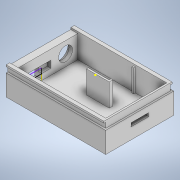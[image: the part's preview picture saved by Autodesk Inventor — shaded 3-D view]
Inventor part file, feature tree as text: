
AUTODESK INVENTOR PART (.ipt)
format: ipt  version: 2021 (Build 250183000, 183)  size: 361,984 bytes
history: native  units: mm
features: sketch x27, extrude x23, other x1
ambient origin geometry x8: Origin, YZ Plane, XZ Plane, XY Plane, X Axis, Y Axis, Z Axis, Center Point
bodies: Body1 (feature_tree)
feature tree (51):
  other  "Sólido1"
  extrude  "Extrusión1"  Depth=35.0mm
  extrude  "Extrusión2"  Depth=51.0mm
  sketch  "Boceto3"  dims[d5=31.0mm d6=13.0mm d7=0.0mm]
  extrude  "Extrusión3"  Depth=13.0mm TaperAngle=0.0deg
  extrude  "Extrusión4"  Depth=15.0mm TaperAngle=0.0deg
  extrude  "Extrusión5"  Depth=6.5mm
  extrude  "Extrusión6"  Depth=2.0mm TaperAngle=0.0deg
  extrude  "Extrusión7"  Depth=2.0mm TaperAngle=0.0deg
  extrude  "Extrusión8"  Depth=32.0mm
  extrude  "Extrusión9"  Depth=13.0mm TaperAngle=0.0deg
  extrude  "Extrusión10"  Depth=15.0mm TaperAngle=0.0deg
  sketch  "Boceto12"  dims[d41=10.0mm d45=3.0mm]
  extrude  "Extrusión11"  Depth=13.0mm TaperAngle=0.0deg
  extrude  "Extrusión12"  Depth=3.0mm
  sketch  "Boceto15"  dims[d55=19.0mm d56=3.0mm]
  sketch  "Boceto16"  dims[d57=2.0mm d58=0.0mm d59=19.5mm]
  extrude  "Extrusión13"  Depth=4.0mm TaperAngle=0.0deg
  extrude  "Extrusión14"  Depth=3.0mm
  extrude  "Extrusión15"  Depth=3.0mm
  extrude  "Extrusión16"  Depth=19.5mm
  extrude  "Extrusión17"  Depth=5.0mm
  extrude  "Extrusión18"  Depth=10.0mm
  extrude  "Extrusión19"  Depth=2.0mm
  extrude  "Extrusión20"  Depth=1.0mm
  extrude  "Extrusión21"  Depth=37.0mm
  extrude  "Extrusión22"  Depth=1.0mm TaperAngle=0.0deg
  sketch  "Boceto26"  dims[d82=0.5mm]
  extrude  "Extrusión23"  Depth=8.0mm
  sketch  "Boceto1"  dims[d0=55.0mm d1=35.0mm]
  sketch  "Boceto2"  dims[d2=15.0mm d3=0.0mm d4=51.0mm]
  sketch  "Boceto4"  dims[d8=2.0mm d9=15.0mm d10=0.0mm]
  sketch  "Boceto5"  dims[d11=9.0mm d12=6.5mm]
  sketch  "Boceto6"  dims[d13=11.0mm d14=2.0mm d15=0.0mm]
  sketch  "Boceto7"  dims[d16=8.0mm d17=2.0mm d18=0.0mm]
  sketch  "Boceto8"  dims[d19=7.0mm d27=32.0mm]
  sketch  "Boceto9"  dims[d28=13.0mm d29=0.0mm d32=13.0mm d33=0.0mm]
  sketch  "Boceto10"  dims[d34=4.0mm d35=15.0mm d36=0.0mm]
  sketch  "Boceto11"  dims[d37=4.0mm d38=13.0mm d39=0.0mm]
  sketch  "Boceto13"  dims[d46=4.0mm d48=4.0mm d49=0.0mm]
  sketch  "Boceto14"  dims[d52=9.5mm d54=3.0mm]
  sketch  "Boceto17"  dims[d60=7.5mm d61=5.0mm]
  sketch  "Boceto18"  dims[d62=1.0mm d63=10.0mm]
  sketch  "Boceto19"  dims[d64=2.0mm d65=2.0mm]
  sketch  "Boceto20"  dims[d66=3.0mm d67=0.0mm d69=1.0mm]
  sketch  "Boceto21"  dims[d70=55.0mm d71=37.0mm]
  sketch  "Boceto22"  dims[d72=3.0mm d73=0.0mm d74=1.0mm d75=0.0mm]
  sketch  "Boceto23"  dims[d76=1.0mm d77=0.0mm d78=8.0mm]
  sketch  "Boceto24"  dims[d79=3.0mm]
  sketch  "Boceto25"  dims[d80=6.0mm d81=0.0mm]
  sketch  "Boceto27"  dims[d83=6.0mm d84=9.0mm d85=6.0mm d86=6.0mm d87=0.0mm d88=1.0mm d89=2.0mm d90=0.0mm d91=100.0mm d92=0.0mm d93=1.0mm d94=0.5mm d95=1.0mm d96=56.0mm d97=0.0mm d98=1.5mm d99=1.0mm d100=2.0mm d101=0.5mm d102=56.0mm d103=0.0mm d104=0.5mm d105=0.5mm d106=56.0mm d107=0.0mm d108=1.0mm d109=0.0mm]
